# Revit family: MCL-G-BO
name_source: partatom
category: Plumbing Fixtures
revit_build: Autodesk Revit 2018 (Build: 20170223_1515(x64)
units: mm (PartAtom-declared; Revit-internal decimal feet)

## family parameters
Always vertical = Yes
Cut with Voids When Loaded = No
Part Type = Normal
Room Calculation Point = No
Round Connector Dimension = Use Diameter
Shared = No
Work Plane-Based = No

## types (8) — shared parameters
Description = BOLT ON (FIXED) EXTENSIONS FOR MCL-G SERIES OF GREASE INTERCEPTORS
Manufacturer = MIFAB
URL = WWW.MIFAB.COM

## per-type parameters (varying)
| type | A-Length | B- Width | E- Height | Model |
| MCL-G-BO-4-6 | 23.75 " | 15.75 " | 6 " | MCL-G-BO-4-6 |
| MCL-G-BO-4-12 | 23.75 " | 15.75 " | 12 " | MCL-G-BO-4-12 |
| MCL-G-BO-5-6 | 27.75 " | 18.75 " | 6 " | MCL-G-BO-5-6 |
| MCL-G-BO-5-12 | 27.75 " | 18.75 " | 12 " | MCL-G-BO-5-6 |
| MCL-G-BO-6-6 | 31.25 " | 23.25 " | 6 " | MCL-G-BO-6-6 |
| MCL-G-BO-6-12 | 31.25 " | 23.25 " | 12 " | MCL-G-BO-6-6 |
| MCL-G-BO-7-6 | 31.25 " | 23.25 " | 6 " | MCL-G-BO-7-6 |
| MCL-G-BO-7-12 | 31.25 " | 23.25 " | 12 " | MCL-G-BO-7-12 |

## geometry (parser evidence)
native form markers: Sweep x2
no freeform markers — native parametric forms only
